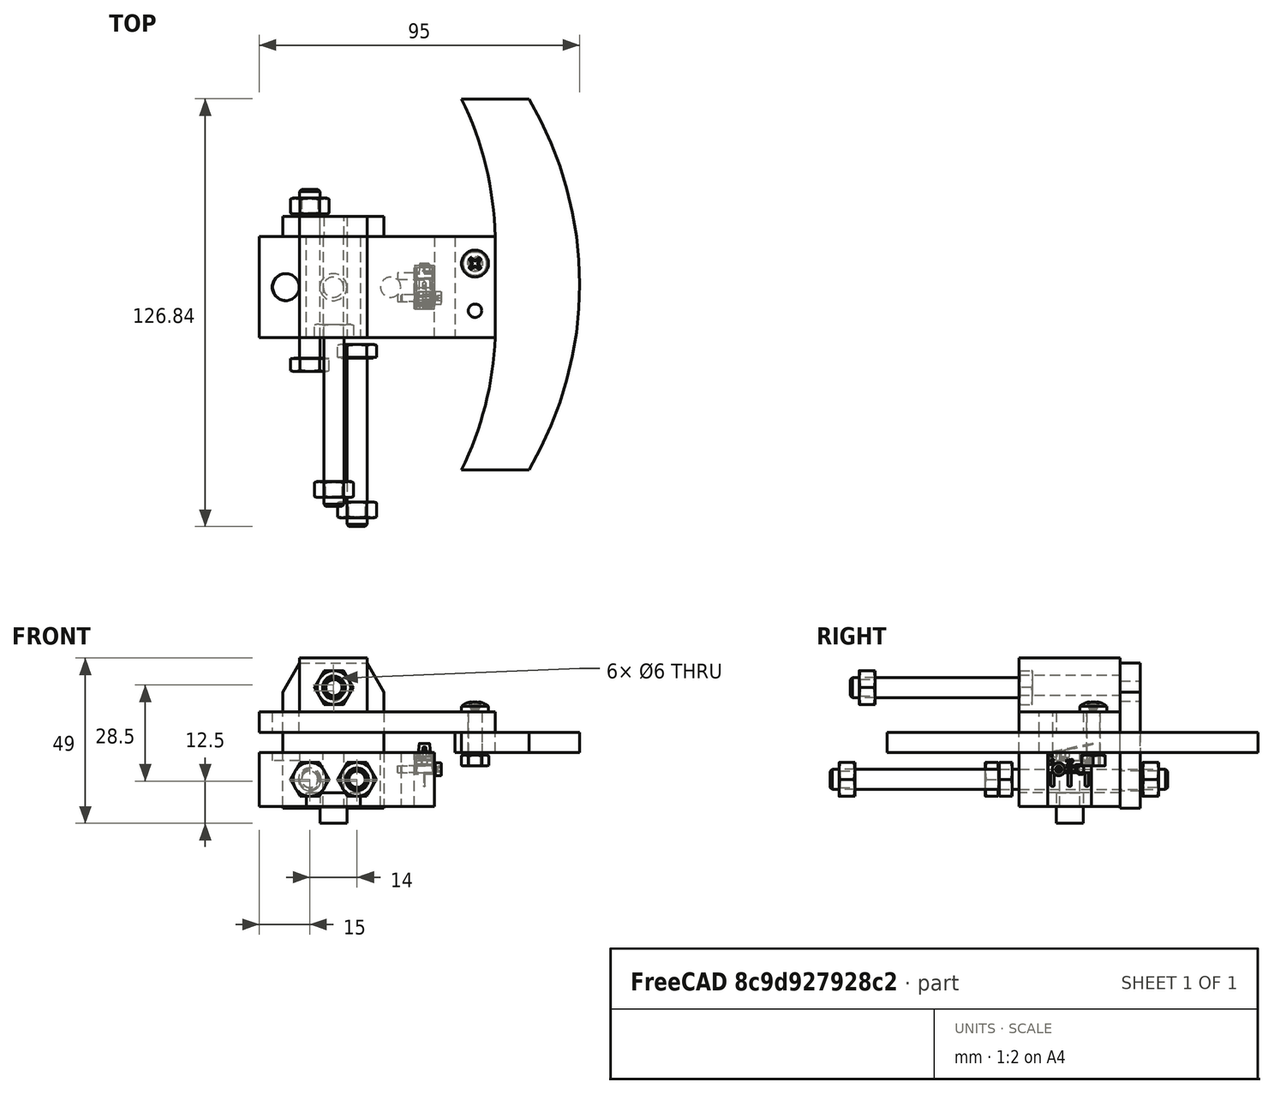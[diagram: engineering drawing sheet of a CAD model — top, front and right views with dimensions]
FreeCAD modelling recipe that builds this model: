
FCSTD DOCUMENT  (FreeCAD 0.19R24267 +99 (Git))
Label: PaddleShifter-v2
License: All rights reserved
LicenseURL: http://en.wikipedia.org/wiki/All_rights_reserved
objects: TechDraw::DrawViewDimension×44, Sketcher::SketchObject×14, Part::FeaturePython×12, TechDraw::DrawProjGroupItem×12, PartDesign::Pocket×10, TechDraw::DrawProjGroup×8, PartDesign::Pad×7, PartDesign::Body×7, PartDesign::SubShapeBinder×3, App::Part×3, PartDesign::ShapeBinder×2, Part::Feature×1, TechDraw::DrawSVGTemplate×1, App::MeasureDistance×1, TechDraw::DrawPage×1, App::DocumentObjectGroup×1
note: 73 computed .brp shape members not serialized (recipe doc carries the construction recipe); baked Part::Feature solids carry a one-line shape summary decoded from their .brp

FEATURE [Part::FeaturePython] Screw006  label="M2x10-Screw001"  # Fasteners workbench fastener (typed FeaturePython)
  Placement = pos=(30,-3.25,11) rot=(0,1,0;1.5708rad)
  baseObject = -> Body [Edge35]
  diameter = 2
  invert = false
  length = 5
  lengthCustom = 10
  matchOuter = true
  offset = 6
  thread = false
  type = 34
FEATURE [Part::FeaturePython] Screw005  label="M2x10-Screw"  # Fasteners workbench fastener (typed FeaturePython)
  Placement = pos=(30,-3.25,11) rot=(0,1,0;1.5708rad)
  baseObject = -> Body [Edge34]
  diameter = 2
  invert = false
  length = 5
  lengthCustom = 10
  matchOuter = true
  offset = 6
  thread = false
  type = 34
FEATURE [Part::FeaturePython] Nut004  label="M6-Nut168"  # Fasteners workbench fastener (typed FeaturePython)
  Placement = pos=(-7,26.3866,8) rot=(1,0,0;1.5708rad)
  baseObject = -> Screw003 [Edge39]
  diameter = 8
  invert = false
  matchOuter = true
  offset = 2
  thread = false
  type = 7
FEATURE [Part::FeaturePython] Nut003  label="M6-Nut167"  # Fasteners workbench fastener (typed FeaturePython)
  Placement = pos=(0.144842,-62.3866,35.2333) rot=(-1,0,0;1.5708rad)
  baseObject = -> Screw004 [Edge39]
  diameter = 8
  invert = false
  matchOuter = true
  offset = 2
  thread = false
  type = 7
FEATURE [Part::FeaturePython] Nut002  label="M6-Nut"  # Fasteners workbench fastener (typed FeaturePython)
  Placement = pos=(7,-68.3866,8) rot=(-1,0,0;1.5708rad)
  baseObject = -> Screw002 [Edge39]
  diameter = 8
  invert = false
  matchOuter = true
  offset = 2
  thread = false
  type = 7
FEATURE [Part::FeaturePython] Screw004  label="M6x50-Screw160"  # Fasteners workbench fastener (typed FeaturePython)
  Placement = pos=(0.144842,-15,35.2333) rot=(-1,0,0;1.5708rad)
  baseObject = -> Body001 [Edge16]
  diameter = 8
  invert = false
  length = 9
  lengthCustom = 50
  matchOuter = true
  offset = 0
  thread = false
  type = 29
FEATURE [Part::FeaturePython] Screw003  label="M6x50-Screw159"  # Fasteners workbench fastener (typed FeaturePython)
  Placement = pos=(-7,-21,8) rot=(1,0,0;1.5708rad)
  baseObject = -> Body001 [Edge17]
  diameter = 8
  invert = false
  length = 9
  lengthCustom = 50
  matchOuter = true
  offset = 0
  thread = false
  type = 29
FEATURE [Part::FeaturePython] Screw002  label="M6x50-Screw"  # Fasteners workbench fastener (typed FeaturePython)
  Placement = pos=(7,-21,8) rot=(-1,0,0;1.5708rad)
  baseObject = -> Body001 [Edge18]
  diameter = 8
  invert = true
  length = 9
  lengthCustom = 50
  matchOuter = true
  offset = 0
  thread = false
  type = 29
FEATURE [Part::Feature] Part__Feature  label="Switch"
  Placement = pos=(27,1.5e-14,9.5) rot=(0,0,1;1.5708rad)
  shape: bbox 7.341 x 13.39 x 13 mm, 256 faces, 7 solids (baked)
FEATURE [PartDesign::ShapeBinder] ShapeBinder001
  Placement = pos=(27,1.5e-14,9.5) rot=(0,0,1;1.5708rad)
  Support = -> [Part__Feature]
  TraceSupport = false
FEATURE [Sketcher::SketchObject] Sketch
  FullyConstrained = true
  MapMode = 5
  Support = -> [XY_Plane001]
  sketch-geometry (10):
    g0: LineSegment StartX=-22 StartY=15 StartZ=0 EndX=30 EndY=15 EndZ=0
    g1: LineSegment StartX=30 StartY=-15 StartZ=0 EndX=-22 EndY=-15 EndZ=0
    g2: LineSegment StartX=-22 StartY=-15 StartZ=0 EndX=-22 EndY=15 EndZ=0
    g3: GeomPoint X=0 Y=15 Z=0
    g4: GeomPoint X=-22 Y=0 Z=0
    g5: LineSegment StartX=30 StartY=15 StartZ=0 EndX=30 EndY=6.5 EndZ=0
    g6: LineSegment StartX=30 StartY=-15 StartZ=0 EndX=30 EndY=-6.5 EndZ=0
    g7: LineSegment StartX=30 StartY=-6.5 StartZ=0 EndX=24 EndY=-6.5 EndZ=0
    g8: LineSegment StartX=24 StartY=-6.5 StartZ=0 EndX=24 EndY=6.5 EndZ=0
    g9: LineSegment StartX=24 StartY=6.5 StartZ=0 EndX=30 EndY=6.5 EndZ=0
  constraints (27):
    c: Coincident(g1,g2)
    c: Coincident(g2,g0)
    c: Horizontal(g0)
    c: Horizontal(g1)
    c: Vertical(g2)
    c: DistanceY(g1,g0) = 30
    c: PointOnObject(g3,g-2)
    c: PointOnObject(g3,g0)
    c: Distance(g3,g0) = 22
    c: Distance(g3,g0) = 30
    c: PointOnObject(g4,g-1)
    c: Symmetric(g0,g1,g4)
    c: Coincident(g5,g0)
    c: Vertical(g5)
    c: Coincident(g6,g1)
    c: Vertical(g6)
    c: Coincident(g7,g6)
    c: Horizontal(g7)
    c: Coincident(g8,g7)
    c: Vertical(g8)
    c: Coincident(g9,g8)
    c: Coincident(g9,g5)
    c: Horizontal(g9)
    c: DistanceY(g8,g8) = 13
    c: Equal(g7,g9)
    c: Equal(g5,g6)
    c: DistanceX(g7,g7) = 6
FEATURE [PartDesign::Pad] Pad
  Direction = (1,1,1)
  Length = 16
  Length2 = 100
  Profile = -> Sketch
  Type = 0
FEATURE [Sketcher::SketchObject] Sketch001
  FullyConstrained = true
  MapMode = 5
  Support = -> [XY_Plane002]
  sketch-geometry (9):
    g0: LineSegment StartX=-15 StartY=21.5 StartZ=0 EndX=15 EndY=21.5 EndZ=0
    g1: LineSegment StartX=15 StartY=21.5 StartZ=0 EndX=15 EndY=-21.5 EndZ=0
    g2: LineSegment StartX=15 StartY=-21.5 StartZ=0 EndX=-15 EndY=-21.5 EndZ=0
    g3: LineSegment StartX=-15 StartY=-21.5 StartZ=0 EndX=-15 EndY=21.5 EndZ=0
    g4: LineSegment StartX=-15 StartY=-21.5 StartZ=0 EndX=-15 EndY=12.8397 EndZ=0
    g5: LineSegment StartX=-15 StartY=12.8397 StartZ=0 EndX=-10 EndY=21.5 EndZ=0
    g6: LineSegment StartX=-10 StartY=21.5 StartZ=0 EndX=10 EndY=21.5 EndZ=0
    g7: LineSegment StartX=10 StartY=21.5 StartZ=0 EndX=15 EndY=12.8397 EndZ=0
    g8: LineSegment StartX=15 StartY=12.8397 StartZ=0 EndX=15 EndY=-21.5 EndZ=0
  constraints (25):
    c: Coincident(g0,g1)
    c: Coincident(g1,g2)
    c: Coincident(g2,g3)
    c: Coincident(g3,g0)
    c: Horizontal(g0)
    c: Horizontal(g2)
    c: Vertical(g1)
    c: Vertical(g3)
    c: Symmetric(g2,g0,g-1)
    c: DistanceX(g0,g0) = 30
    c: DistanceY(g1,g1) = 43
    c: Coincident(g4,g2)
    c: PointOnObject(g4,g3)
    c: Coincident(g5,g4)
    c: PointOnObject(g5,g0)
    c: Coincident(g6,g5)
    c: PointOnObject(g6,g0)
    c: Coincident(g7,g6)
    c: PointOnObject(g7,g1)
    c: Coincident(g8,g7)
    c: Coincident(g8,g2)
    c: Equal(g4,g8)
    c: Equal(g5,g7)
    c: Distance(g6) = 20
    c: Distance(g7) = 10
FEATURE [PartDesign::Pad] Pad001
  Direction = (1,1,1)
  Length = 6
  Length2 = 100
  Profile = -> Sketch001
  Type = 0
FEATURE [PartDesign::SubShapeBinder] Binder
  BindMode = 0
  ClaimChildren = false
  Context = -> Part [Body001.Binder.]
  Fuse = false
  MakeFace = true
  PartialLoad = false
  Relative = true
  Support = -> [Part001[Body004.Pocket002.Edge15]]
  _Version = 2
FEATURE [PartDesign::Pocket] Pocket008
  BaseFeature = -> Pad001
  Length = 5
  Length2 = 100
  Profile = -> Binder
  Reversed = true
  Type = 1
FEATURE [Sketcher::SketchObject] Sketch012
  FullyConstrained = false
  MapMode = 5
  Support = -> [XY_Plane009]
  sketch-geometry (13):
    g0: LineSegment StartX=-10 StartY=55 StartZ=0 EndX=10 EndY=55 EndZ=0
    g1: LineSegment StartX=10 StartY=55 StartZ=0 EndX=10 EndY=-55 EndZ=0
    g2: LineSegment StartX=10 StartY=-55 StartZ=0 EndX=-10 EndY=-55 EndZ=0
    g3: LineSegment StartX=-10 StartY=-55 StartZ=0 EndX=-10 EndY=55 EndZ=0
    g4: LineSegment StartX=10 StartY=55 StartZ=0 EndX=-10 EndY=55 EndZ=0
    g5: LineSegment StartX=0 StartY=14.1646 StartZ=0 EndX=-12 EndY=14.1646 EndZ=0
    g6: LineSegment StartX=7e-16 StartY=-15.8354 StartZ=0 EndX=-12 EndY=-15.8354 EndZ=0
    g7: LineSegment StartX=-12 StartY=14.1646 StartZ=0 EndX=-12 EndY=-15.8354 EndZ=0
    g8: LineSegment StartX=10 StartY=-55 StartZ=0 EndX=-10 EndY=-55 EndZ=0
    g9: ArcOfCircle CenterX=-83.3333 CenterY=1e-15 CenterZ=0 NormalX=0 NormalY=0 NormalZ=1 AngleXU=0 Radius=108.333 StartAngle=5.75068 EndAngle=6.81569
    g10: ArcOfCircle CenterX=-98.5179 CenterY=-11.5395 CenterZ=0 NormalX=0 NormalY=0 NormalZ=1 AngleXU=0 Radius=98.6115 StartAngle=5.82678 EndAngle=6.23961
    g11: ArcOfCircle CenterX=-98.5798 CenterY=11.666 CenterZ=0 NormalX=0 NormalY=0 NormalZ=1 AngleXU=0 Radius=98.6115 StartAngle=0.025341 EndAngle=0.454978
    g12: GeomPoint X=25 Y=0 Z=0
  constraints (34):
    c: Coincident(g0,g1)
    c: Coincident(g2,g3)
    c: Coincident(g3,g0)
    c: Horizontal(g0)
    c: Horizontal(g2)
    c: Coincident(g7,g5)
    c: Coincident(g7,g6)
    c: Equal(g5,g6)
    c: Vertical(g7)
    c: Coincident(g8,g2)
    c: Horizontal(g5)
    c: Horizontal(g6)
    c: Coincident(g4,g0)
    c: DistanceX(g0,g0) = 20
    c: PointOnObject(g5,g-2)
    c: DistanceY(g7,g7) = 30
    c: Coincident(g9,g4)
    c: Vertical(g3)
    c: Vertical(g1)
    c: Coincident(g10,g6)
    c: Coincident(g10,g8)
    c: Coincident(g11,g4)
    c: Coincident(g11,g5)
    c: Equal(g11,g10)
    c: DistanceY(g8,g4) = 110
    c: PointOnObject(g12,g9)
    c: PointOnObject(g12,g-1)
    c: Distance(g-1,g12) = 25
    c: DistanceX(g5,g5) = 12
    c: Coincident(g8,g1)
    c: Coincident(g8,g9)
    c: Coincident(g8,g2)
    c: Coincident(g4,g0)
    c: Symmetric(g8,g4,g-1)
FEATURE [PartDesign::Pad] Pad006
  Direction = (1,1,1)
  Length = 6
  Length2 = 100
  Profile = -> Sketch012
  Type = 0
FEATURE [Sketcher::SketchObject] Sketch014
  ExternalGeometry = -> [Pad006]
  FullyConstrained = true
  MapMode = 5
  Placement = pos=(0,0,6) rot=(0,0,1;0rad)
  Support = -> [Pad006]
  sketch-geometry (3):
    g0: Circle CenterX=-6 CenterY=6.1646 CenterZ=0 NormalX=0 NormalY=0 NormalZ=1 AngleXU=0 Radius=2
    g1: Circle CenterX=-6 CenterY=-7.8354 CenterZ=0 NormalX=0 NormalY=0 NormalZ=1 AngleXU=0 Radius=2
    g2: LineSegment StartX=-6 StartY=14.1646 StartZ=0 EndX=-6 EndY=-15.8354 EndZ=0
  constraints (10):
    c: Equal(g0,g1)
    c: Diameter(g0) = 4
    c: PointOnObject(g2,g-3)
    c: PointOnObject(g2,g-5)
    c: Vertical(g2)
    c: PointOnObject(g0,g2)
    c: PointOnObject(g1,g2)
    c: Distance(g0,g2) = 8
    c: Distance(g1,g2) = 8
    c: Distance(g2,g-4) = 6
FEATURE [PartDesign::Pocket] Pocket007
  BaseFeature = -> Pad006
  Length = 5
  Length2 = 100
  Profile = -> Sketch014
  Type = 1
FEATURE [PartDesign::Body] Body006  label="Лепесток"
  Group = -> [Sketch012,Pad006,Sketch014,Pocket007]
  Origin = -> Origin009
  Placement = pos=(48,0.8354,16) rot=(0,0,1;0rad)
  Tip = -> Pocket007
FEATURE [Sketcher::SketchObject] Sketch007
  FullyConstrained = true
  MapMode = 5
  Support = -> [XY_Plane005]
  sketch-geometry (4):
    g0: LineSegment StartX=-10 StartY=15 StartZ=0 EndX=10 EndY=15 EndZ=0
    g1: LineSegment StartX=10 StartY=15 StartZ=0 EndX=10 EndY=-15 EndZ=0
    g2: LineSegment StartX=10 StartY=-15 StartZ=0 EndX=-10 EndY=-15 EndZ=0
    g3: LineSegment StartX=-10 StartY=-15 StartZ=0 EndX=-10 EndY=15 EndZ=0
  constraints (11):
    c: Coincident(g0,g1)
    c: Coincident(g1,g2)
    c: Coincident(g2,g3)
    c: Coincident(g3,g0)
    c: Horizontal(g0)
    c: Horizontal(g2)
    c: Vertical(g1)
    c: Vertical(g3)
    c: Symmetric(g0,g2,g-1)
    c: DistanceX(g0,g0) = 20
    c: DistanceY(g1,g1) = 30
FEATURE [PartDesign::Pad] Pad004
  Direction = (1,1,1)
  Length = 16
  Length2 = 100
  Profile = -> Sketch007
  Type = 0
FEATURE [Sketcher::SketchObject] Sketch008
  ExternalGeometry = -> [Pad004]
  FullyConstrained = true
  MapMode = 5
  Placement = pos=(0,15,0) rot=(0,0.707107,0.707107;3.14159rad)
  Support = -> [Pad004]
  sketch-geometry (1):
    g0: Circle CenterX=1.1e-15 CenterY=8 CenterZ=0 NormalX=0 NormalY=0 NormalZ=1 AngleXU=0 Radius=3
  constraints (2):
    c: Diameter(g0) = 6
    c: Symmetric(g-3,g-5,g0)
FEATURE [PartDesign::Pocket] Pocket002
  BaseFeature = -> Pad004
  Length = 5
  Length2 = 100
  Profile = -> Sketch008
  Type = 1
FEATURE [PartDesign::Body] Body004  label="Крепление рычага"
  Group = -> [Sketch007,Pad004,Sketch008,Pocket002]
  Origin = -> Origin005
  Placement = pos=(0,0,28) rot=(0,0,1;0rad)
  Tip = -> Pocket002
FEATURE [Sketcher::SketchObject] Sketch005
  FullyConstrained = true
  MapMode = 5
  Support = -> [XY_Plane003]
  sketch-geometry (4):
    g0: LineSegment StartX=-35 StartY=15 StartZ=0 EndX=35 EndY=15 EndZ=0
    g1: LineSegment StartX=35 StartY=15 StartZ=0 EndX=35 EndY=-15 EndZ=0
    g2: LineSegment StartX=35 StartY=-15 StartZ=0 EndX=-35 EndY=-15 EndZ=0
    g3: LineSegment StartX=-35 StartY=-15 StartZ=0 EndX=-35 EndY=15 EndZ=0
  constraints (11):
    c: Coincident(g0,g1)
    c: Coincident(g1,g2)
    c: Coincident(g2,g3)
    c: Coincident(g3,g0)
    c: Horizontal(g0)
    c: Horizontal(g2)
    c: Vertical(g1)
    c: Vertical(g3)
    c: Symmetric(g0,g2,g-1)
    c: DistanceY(g1,g1) = 30
    c: DistanceX(g0,g0) = 70
FEATURE [PartDesign::Pad] Pad002
  Direction = (1,1,1)
  Length = 6
  Length2 = 100
  Profile = -> Sketch005
  Type = 0
FEATURE [PartDesign::SubShapeBinder] Binder001
  BindMode = 0
  ClaimChildren = false
  Context = -> Part [Part001.Body002.Binder001.]
  Fuse = false
  MakeFace = true
  PartialLoad = false
  Relative = true
  Support = -> [Part002[Body003.Pad003.Edge15]]
  _Version = 2
FEATURE [PartDesign::Pocket] Pocket004
  BaseFeature = -> Pad002
  Length = 5
  Length2 = 100
  Profile = -> Binder001
  Reversed = true
  Type = 1
FEATURE [Sketcher::SketchObject] Sketch013
  ExternalGeometry = -> [Pocket004]
  FullyConstrained = false
  MapMode = 5
  Placement = pos=(0,0,6) rot=(0,0,1;0rad)
  Support = -> [Pocket004]
  sketch-geometry (3):
    g0: Circle CenterX=29 CenterY=7 CenterZ=0 NormalX=0 NormalY=0 NormalZ=1 AngleXU=0 Radius=2
    g1: Circle CenterX=29 CenterY=-7 CenterZ=0 NormalX=0 NormalY=0 NormalZ=1 AngleXU=0 Radius=2
    g2: LineSegment StartX=29 StartY=15 StartZ=0 EndX=29 EndY=-15 EndZ=0
  constraints (9):
    c: Diameter(g0) = 4
    c: Equal(g0,g1)
    c: PointOnObject(g2,g-3)
    c: Vertical(g2)
    c: PointOnObject(g0,g2)
    c: PointOnObject(g1,g2)
    c: Distance(g0,g2) = 8
    c: Distance(g1,g2) = 8
    c: Distance(g2,g-3) = 6
FEATURE [PartDesign::Pocket] Pocket006
  BaseFeature = -> Pocket004
  Length = 5
  Length2 = 100
  Profile = -> Sketch013
  Type = 1
FEATURE [PartDesign::Body] Body002  label="Рычаг"
  Group = -> [Sketch005,Pad002,Binder001,Pocket004,Sketch013,Pocket006]
  Origin = -> Origin003
  Placement = pos=(13,0,22) rot=(0,0,1;0rad)
  Tip = -> Pocket006
FEATURE [Sketcher::SketchObject] Sketch006
  FullyConstrained = true
  MapMode = 5
  Support = -> [XY_Plane004]
  sketch-geometry (5):
    g0: LineSegment StartX=-8 StartY=15 StartZ=0 EndX=8 EndY=15 EndZ=0
    g1: LineSegment StartX=8 StartY=15 StartZ=0 EndX=8 EndY=-15 EndZ=0
    g2: LineSegment StartX=8 StartY=-15 StartZ=0 EndX=-8 EndY=-15 EndZ=0
    g3: LineSegment StartX=-8 StartY=-15 StartZ=0 EndX=-8 EndY=15 EndZ=0
    g4: Circle CenterX=0 CenterY=0 CenterZ=0 NormalX=0 NormalY=0 NormalZ=1 AngleXU=0 Radius=4
  constraints (13):
    c: Coincident(g0,g1)
    c: Coincident(g1,g2)
    c: Coincident(g2,g3)
    c: Coincident(g3,g0)
    c: Horizontal(g0)
    c: Horizontal(g2)
    c: Vertical(g1)
    c: Vertical(g3)
    c: Symmetric(g0,g2,g-1)
    c: DistanceX(g0,g0) = 16
    c: DistanceY(g1,g1) = 30
    c: Coincident(g4,g-1)
    c: Diameter(g4) = 8
FEATURE [PartDesign::Pad] Pad003
  Direction = (1,1,1)
  Length = 4
  Length2 = 100
  Midplane = true
  Profile = -> Sketch006
  Type = 0
FEATURE [PartDesign::Body] Body003  label="Проставка"
  Group = -> [Sketch006,Pad003]
  Origin = -> Origin004
  Placement = pos=(0,0,2) rot=(0,0,1;0rad)
  Tip = -> Pad003
FEATURE [Sketcher::SketchObject] Sketch010
  FullyConstrained = true
  MapMode = 5
  Support = -> [XY_Plane007]
  sketch-geometry (1):
    g0: Circle CenterX=0 CenterY=0 CenterZ=0 NormalX=0 NormalY=0 NormalZ=1 AngleXU=0 Radius=4
  constraints (2):
    c: Coincident(g0,g-1)
    c: Diameter(g0) = 8
FEATURE [PartDesign::Pad] Pad005
  Direction = (1,1,1)
  Length = 5
  Length2 = 100
  Profile = -> Sketch010
  Type = 0
FEATURE [PartDesign::Body] Body005  label="Неодимовый магнит (8х5)"
  Group = -> [Sketch010,Pad005]
  Origin = -> Origin007
  Placement = pos=(-14,0,22) rot=(0,0,1;0rad)
  Tip = -> Pad005
FEATURE [Part::FeaturePython] Clone  label="Неодимовый магнит (8х5)001"  # Draft clone (typed FeaturePython)
  AttacherType = Attacher::AttachEngine3D
  Fuse = false
  Objects = -> [Body005]
  Placement = pos=(4e-15,0,-5) rot=(0,0,1;0rad)
  Scale = (1,1,1)
FEATURE [App::Part] Part002  label="Проставка001"
  Group = -> [Clone,Body003]
  Origin = -> Origin008
  Placement = pos=(-14,0,16) rot=(0,0,1;0rad)
FEATURE [Part::FeaturePython] Screw  label="M4x16-Screw"  # Fasteners workbench fastener (typed FeaturePython)
  Placement = pos=(42,7,28) rot=(0,0,1;0rad)
  baseObject = -> Body002 [Edge18]
  diameter = 6
  invert = false
  length = 6
  lengthCustom = 16
  matchOuter = false
  offset = 0
  thread = false
  type = 35
FEATURE [Part::FeaturePython] Nut005  label="M4-Nut"  # Fasteners workbench fastener (typed FeaturePython)
  Placement = pos=(42,7,12) rot=(0,0,1;0rad)
  baseObject = -> Screw [Edge7]
  diameter = 6
  invert = false
  matchOuter = false
  offset = 0
  thread = false
  type = 7
FEATURE [App::Part] Part001  label="Рычаг001"
  Group = -> [Body002,Body004,Body005,Body006,Screw,Nut005]
  Origin = -> Origin006
  Placement = pos=(0.144842,0,-0.766663) rot=(0,0,1;0rad)
FEATURE [PartDesign::SubShapeBinder] Binder002
  BindMode = 0
  ClaimChildren = false
  Context = -> Part [Body.Binder002.]
  Fuse = false
  MakeFace = true
  PartialLoad = false
  Relative = true
  Support = -> [Part002[Body003.Pad003.Edge14]]
  _Version = 2
FEATURE [Sketcher::SketchObject] Sketch015
  ExternalGeometry = -> [Pocket008]
  FullyConstrained = true
  MapMode = 5
  Placement = pos=(0,0,6) rot=(0,0,1;0rad)
  Support = -> [Pocket008]
  sketch-geometry (3):
    g0: LineSegment StartX=-15 StartY=-13.5 StartZ=0 EndX=15 EndY=-13.5 EndZ=0
    g1: Circle CenterX=-7 CenterY=-13.5 CenterZ=0 NormalX=0 NormalY=0 NormalZ=1 AngleXU=0 Radius=3
    g2: Circle CenterX=7 CenterY=-13.5 CenterZ=0 NormalX=0 NormalY=0 NormalZ=1 AngleXU=0 Radius=3
  constraints (10):
    c: PointOnObject(g0,g-3)
    c: PointOnObject(g0,g-5)
    c: Horizontal(g0)
    c: PointOnObject(g1,g0)
    c: PointOnObject(g2,g0)
    c: Equal(g2,g1)
    c: Diameter(g2) = 6
    c: DistanceY(g-5,g0) = 8
    c: Distance(g2,g-5) = 8
    c: Distance(g1,g-3) = 8
FEATURE [PartDesign::Pocket] Pocket
  BaseFeature = -> Pocket008
  Length = 5
  Length2 = 100
  Profile = -> Sketch015
  Type = 1
FEATURE [PartDesign::Body] Body001  label="Крепление"
  Group = -> [Sketch001,Pad001,Binder,Pocket008,Sketch015,Pocket]
  Origin = -> Origin002
  Placement = pos=(-3e-15,-15,22) rot=(1,0,0;1.5708rad)
  Tip = -> Pocket
FEATURE [PartDesign::ShapeBinder] ShapeBinder
  Placement = pos=(-3e-15,-15,22) rot=(1,0,0;1.5708rad)
  Support = -> [Body001]
  TraceSupport = false
FEATURE [Sketcher::SketchObject] Sketch004
  ExternalGeometry = -> [ShapeBinder]
  FullyConstrained = false
  MapMode = 5
  Placement = pos=(0,15,0) rot=(0,0.707107,0.707107;3.14159rad)
  Support = -> [Pad]
  sketch-geometry (3):
    g0: Circle CenterX=7 CenterY=8 CenterZ=0 NormalX=0 NormalY=0 NormalZ=1 AngleXU=0 Radius=3
    g1: Circle CenterX=-9e-16 CenterY=31 CenterZ=0 NormalX=0 NormalY=0 NormalZ=1 AngleXU=0 Radius=3
    g2: Circle CenterX=-7 CenterY=8 CenterZ=0 NormalX=0 NormalY=0 NormalZ=1 AngleXU=0 Radius=3
FEATURE [PartDesign::Pocket] Pocket001
  BaseFeature = -> Pad
  Length = 5
  Length2 = 100
  Profile = -> Sketch004
  Type = 1
FEATURE [Sketcher::SketchObject] Sketch009
  ExternalGeometry = -> [Pocket001]
  FullyConstrained = true
  MapMode = 5
  Placement = pos=(0,0,16) rot=(0,0,1;0rad)
  Support = -> [Pocket001]
  sketch-geometry (2):
    g0: Circle CenterX=0 CenterY=0 CenterZ=0 NormalX=0 NormalY=0 NormalZ=1 AngleXU=0 Radius=3
    g1: Circle CenterX=17 CenterY=0 CenterZ=0 NormalX=0 NormalY=0 NormalZ=1 AngleXU=0 Radius=3
  constraints (5):
    c: Diameter(g0) = 6
    c: PointOnObject(g1,g-1)
    c: Equal(g0,g1)
    c: Distance(g1,g-6) = 13
    c: Coincident(g0,g-1)
FEATURE [PartDesign::Pocket] Pocket003
  BaseFeature = -> Pocket001
  Length = 5
  Length2 = 100
  Profile = -> Sketch009
  Type = 1
FEATURE [Sketcher::SketchObject] Sketch011
  ExternalGeometry = -> [Pocket003]
  FullyConstrained = true
  MapMode = 5
  Placement = pos=(24,0,0) rot=(0.57735,0.57735,0.57735;2.0944rad)
  Support = -> [Pocket003]
  sketch-geometry (3):
    g0: Circle CenterX=3.25 CenterY=11 CenterZ=0 NormalX=0 NormalY=0 NormalZ=1 AngleXU=0 Radius=1
    g1: Circle CenterX=-3.25 CenterY=11 CenterZ=0 NormalX=0 NormalY=0 NormalZ=1 AngleXU=0 Radius=1
    g2: LineSegment StartX=-3.25 StartY=11 StartZ=0 EndX=3.25 EndY=11 EndZ=0
  constraints (8):
    c: Diameter(g0) = 2
    c: DistanceX(g-2,g0) = 3.25
    c: Equal(g1,g0)
    c: Coincident(g2,g1)
    c: Coincident(g2,g0)
    c: Horizontal(g2)
    c: DistanceX(g-2,g1) = -3.25
    c: Distance(g1,g-3) = 5
FEATURE [PartDesign::Pocket] Pocket005
  BaseFeature = -> Pocket003
  Length = 5
  Length2 = 100
  Profile = -> Sketch011
  Type = 0
FEATURE [Part::FeaturePython] Clone001  label="Крепление001"  # Draft clone (typed FeaturePython)
  AttacherType = Attacher::AttachEngine3D
  Fuse = false
  Objects = -> [Body001]
  Placement = pos=(-3e-15,21,21) rot=(1,0,0;1.5708rad)
  Scale = (1,1,1)
FEATURE [PartDesign::Pocket] Pocket009
  BaseFeature = -> Pocket005
  Length = 5
  Length2 = 100
  Midplane = true
  Profile = -> Binder002
  Type = 0
FEATURE [PartDesign::Body] Body  label="Основа"
  Group = -> [Sketch,Pad,ShapeBinder,Sketch004,Pocket001,Sketch009,Pocket003,ShapeBinder001,Sketch011,Pocket005,Binder002,Pocket009]
  Origin = -> Origin001
  Tip = -> Pocket009
FEATURE [App::Part] Part  label="PaddleShifter"
  Group = -> [Body,Body001,Part__Feature,Part001,Part002,Screw002,Screw003,Screw004,Nut002,Nut003,Nut004,Screw005,Screw006,Clone001]
  Origin = -> Origin
FEATURE [TechDraw::DrawSVGTemplate] Template
  Height = 210
  Orientation = 1
  Width = 297
FEATURE [TechDraw::DrawProjGroupItem] ProjItem  label="Front"
  CoarseView = false
  Direction = (0,-1,0)
  Focus = 100
  HardHidden = false
  IsoCount = 0
  IsoHidden = false
  IsoVisible = false
  LockPosition = true
  Perspective = false
  Rotation = 0
  RotationVector = (1,0,0)
  ScaleType = 2
  SeamHidden = false
  SeamVisible = true
  SmoothHidden = false
  SmoothVisible = true
  Source = -> [Body001]
  Type = 0
  X = 0
  XDirection = (1,0,0)
  Y = 0
FEATURE [TechDraw::DrawProjGroupItem] ProjItem001  label="Left"
  CoarseView = false
  Direction = (-1,-1e-16,0)
  Focus = 100
  HardHidden = false
  IsoCount = 0
  IsoHidden = false
  IsoVisible = false
  LockPosition = false
  Perspective = false
  Rotation = 0
  RotationVector = (1,0,0)
  ScaleType = 2
  SeamHidden = false
  SeamVisible = true
  SmoothHidden = false
  SmoothVisible = true
  Source = -> [Body001]
  Type = 1
  X = 33
  XDirection = (1e-16,-1,0)
  Y = 0
FEATURE [TechDraw::DrawProjGroup] ProjGroup
  Anchor = -> ProjItem
  AutoDistribute = true
  LockPosition = false
  ProjectionType = 0
  Rotation = 0
  ScaleType = 0
  Source = -> [Body001]
  Views = -> [ProjItem,ProjItem001]
  X = 43.5
  Y = 172.616
  spacingX = 15
  spacingY = 15
FEATURE [TechDraw::DrawProjGroupItem] ProjItem002  label="Front001"
  CoarseView = false
  Direction = (0,-1,0)
  Focus = 100
  HardHidden = false
  IsoCount = 0
  IsoHidden = false
  IsoVisible = false
  LockPosition = true
  Perspective = false
  Rotation = 0
  RotationVector = (1,0,0)
  ScaleType = 2
  SeamHidden = false
  SeamVisible = true
  SmoothHidden = false
  SmoothVisible = true
  Source = -> [Body]
  Type = 0
  X = 0
  XDirection = (1,0,0)
  Y = 0
FEATURE [TechDraw::DrawProjGroupItem] ProjItem004  label="Front002"
  CoarseView = false
  Direction = (0,0,1)
  Focus = 100
  HardHidden = false
  IsoCount = 0
  IsoHidden = false
  IsoVisible = false
  LockPosition = true
  Perspective = false
  Rotation = 0
  RotationVector = (1,0,0)
  ScaleType = 2
  SeamHidden = false
  SeamVisible = true
  SmoothHidden = false
  SmoothVisible = true
  Source = -> [Body004]
  Type = 0
  X = 0
  XDirection = (1,0,0)
  Y = 0
FEATURE [TechDraw::DrawProjGroupItem] ProjItem005  label="Top"
  CoarseView = false
  Direction = (0,1,0)
  Focus = 100
  HardHidden = false
  IsoCount = 0
  IsoHidden = false
  IsoVisible = false
  LockPosition = false
  Perspective = false
  Rotation = 0
  RotationVector = (1,0,0)
  ScaleType = 2
  SeamHidden = false
  SeamVisible = true
  SmoothHidden = false
  SmoothVisible = true
  Source = -> [Body004]
  Type = 4
  X = 0
  XDirection = (1,0,0)
  Y = -52
FEATURE [TechDraw::DrawProjGroup] ProjGroup002
  Anchor = -> ProjItem004
  AutoDistribute = true
  LockPosition = false
  ProjectionType = 0
  Rotation = 0
  ScaleType = 0
  Source = -> [Body004]
  Views = -> [ProjItem004,ProjItem005]
  X = 193.036
  Y = 170.341
  spacingX = 15
  spacingY = 15
FEATURE [TechDraw::DrawProjGroupItem] ProjItem006  label="Front003"
  CoarseView = false
  Direction = (0,0,1)
  Focus = 100
  HardHidden = false
  IsoCount = 0
  IsoHidden = false
  IsoVisible = false
  LockPosition = true
  Perspective = false
  Rotation = 0
  RotationVector = (1,0,0)
  ScaleType = 2
  SeamHidden = false
  SeamVisible = true
  SmoothHidden = false
  SmoothVisible = true
  Source = -> [Body002]
  Type = 0
  X = 0
  XDirection = (1,0,0)
  Y = 0
FEATURE [TechDraw::DrawProjGroup] ProjGroup003
  Anchor = -> ProjItem006
  AutoDistribute = true
  LockPosition = false
  ProjectionType = 0
  Rotation = 0
  ScaleType = 0
  Source = -> [Body002]
  Views = -> [ProjItem006]
  X = 61.3793
  Y = 113.127
  spacingX = 15
  spacingY = 15
FEATURE [TechDraw::DrawProjGroupItem] ProjItem007  label="Top001"
  CoarseView = false
  Direction = (0,0,1)
  Focus = 100
  HardHidden = false
  IsoCount = 0
  IsoHidden = false
  IsoVisible = false
  LockPosition = false
  Perspective = false
  Rotation = 0
  RotationVector = (1,0,0)
  ScaleType = 2
  SeamHidden = false
  SeamVisible = true
  SmoothHidden = false
  SmoothVisible = true
  Source = -> [Body]
  Type = 4
  X = 0
  XDirection = (1,0,0)
  Y = -45
FEATURE [TechDraw::DrawProjGroup] ProjGroup001
  Anchor = -> ProjItem002
  AutoDistribute = true
  LockPosition = false
  ProjectionType = 0
  Rotation = 0
  ScaleType = 0
  Source = -> [Body]
  Views = -> [ProjItem002,ProjItem007]
  X = 135.497
  Y = 122.554
  spacingX = 15
  spacingY = 15
FEATURE [TechDraw::DrawProjGroupItem] ProjItem008  label="Front004"
  CoarseView = false
  Direction = (0,0,1)
  Focus = 100
  HardHidden = false
  IsoCount = 0
  IsoHidden = false
  IsoVisible = false
  LockPosition = true
  Perspective = false
  Rotation = 0
  RotationVector = (1,0,0)
  ScaleType = 2
  SeamHidden = false
  SeamVisible = true
  SmoothHidden = false
  SmoothVisible = true
  Source = -> [Body006]
  Type = 0
  X = 0
  XDirection = (-2e-16,1,0)
  Y = 0
FEATURE [TechDraw::DrawProjGroup] ProjGroup004
  Anchor = -> ProjItem008
  AutoDistribute = true
  LockPosition = false
  ProjectionType = 0
  Rotation = 0
  ScaleType = 0
  Source = -> [Body006]
  Views = -> [ProjItem008]
  X = 71.2141
  Y = 35.5674
  spacingX = 15
  spacingY = 15
FEATURE [TechDraw::DrawProjGroupItem] ProjItem009  label="Front005"
  CoarseView = false
  Direction = (0,0,1)
  Focus = 100
  HardHidden = false
  IsoCount = 0
  IsoHidden = false
  IsoVisible = false
  LockPosition = true
  Perspective = false
  Rotation = 0
  RotationVector = (1,0,0)
  ScaleType = 2
  SeamHidden = false
  SeamVisible = true
  SmoothHidden = false
  SmoothVisible = true
  Source = -> [Part002]
  Type = 0
  X = 0
  XDirection = (1,0,0)
  Y = 0
FEATURE [TechDraw::DrawProjGroupItem] ProjItem010  label="Top002"
  CoarseView = false
  Direction = (0,1,0)
  Focus = 100
  HardHidden = false
  IsoCount = 0
  IsoHidden = false
  IsoVisible = false
  LockPosition = false
  Perspective = false
  Rotation = 0
  RotationVector = (1,0,0)
  ScaleType = 2
  SeamHidden = false
  SeamVisible = true
  SmoothHidden = false
  SmoothVisible = true
  Source = -> [Part002]
  Type = 4
  X = 0
  XDirection = (1,0,0)
  Y = -55.5
FEATURE [TechDraw::DrawProjGroup] ProjGroup005
  Anchor = -> ProjItem009
  AutoDistribute = true
  LockPosition = false
  ProjectionType = 0
  Rotation = 0
  ScaleType = 0
  Source = -> [Part002]
  Views = -> [ProjItem009,ProjItem010]
  X = 238.238
  Y = 169.811
  spacingX = 15
  spacingY = 15
FEATURE [TechDraw::DrawProjGroupItem] ProjItem011  label="Front006"
  CoarseView = false
  Direction = (0,0,1)
  Focus = 100
  HardHidden = false
  IsoCount = 0
  IsoHidden = false
  IsoVisible = false
  LockPosition = true
  Perspective = false
  Rotation = 0
  RotationVector = (1,0,0)
  ScaleType = 2
  SeamHidden = false
  SeamVisible = true
  SmoothHidden = false
  SmoothVisible = true
  Source = -> [Body006]
  Type = 0
  X = 0
  XDirection = (-2e-16,1,0)
  Y = 0
FEATURE [TechDraw::DrawProjGroup] ProjGroup006
  Anchor = -> ProjItem011
  AutoDistribute = true
  LockPosition = false
  ProjectionType = 0
  Rotation = 0
  ScaleType = 0
  Source = -> [Body006]
  Views = -> [ProjItem011]
  X = 209.746
  Y = 38.0976
  spacingX = 15
  spacingY = 15
FEATURE [TechDraw::DrawViewDimension] Dimension
  Arbitrary = false
  ArbitraryTolerances = false
  EqualTolerance = true
  FormatSpec = %.2f
  FormatSpecOverTolerance = %+.2f
  FormatSpecUnderTolerance = %+.2f
  Inverted = false
  LockPosition = false
  MeasureType = 1
  OverTolerance = 0
  References2D = -> [ProjItem]
  Rotation = 0
  ScaleType = 0
  TheoreticalExact = false
  Type = 2
  UnderTolerance = 0
  X = 19.8762
  Y = -4.33013
FEATURE [TechDraw::DrawViewDimension] Dimension002
  Arbitrary = false
  ArbitraryTolerances = false
  EqualTolerance = true
  FormatSpec = %.2f
  FormatSpecOverTolerance = %+.2f
  FormatSpecUnderTolerance = %+.2f
  Inverted = false
  LockPosition = false
  MeasureType = 1
  OverTolerance = 0
  References2D = -> [ProjItem]
  Rotation = 0
  ScaleType = 0
  TheoreticalExact = false
  Type = 2
  UnderTolerance = 0
  X = -21.9814
  Y = 0.270898
FEATURE [TechDraw::DrawViewDimension] Dimension003
  Arbitrary = false
  ArbitraryTolerances = false
  EqualTolerance = true
  FormatSpec = %.2f
  FormatSpecOverTolerance = %+.2f
  FormatSpecUnderTolerance = %+.2f
  Inverted = false
  LockPosition = false
  MeasureType = 1
  OverTolerance = 0
  References2D = -> [ProjItem]
  Rotation = 0
  ScaleType = 0
  TheoreticalExact = false
  Type = 2
  UnderTolerance = 0
  X = 19.2724
  Y = 17.5662
FEATURE [TechDraw::DrawViewDimension] Dimension004
  Arbitrary = false
  ArbitraryTolerances = false
  EqualTolerance = true
  FormatSpec = %.2f
  FormatSpecOverTolerance = %+.2f
  FormatSpecUnderTolerance = %+.2f
  Inverted = false
  LockPosition = false
  MeasureType = 1
  OverTolerance = 0
  References2D = -> [ProjItem]
  Rotation = 0
  ScaleType = 0
  TheoreticalExact = false
  Type = 1
  UnderTolerance = 0
  X = 0
  Y = -21.3739
FEATURE [TechDraw::DrawViewDimension] Dimension005
  Arbitrary = false
  ArbitraryTolerances = false
  EqualTolerance = true
  FormatSpec = ⌀%.2f
  FormatSpecOverTolerance = %+.2f
  FormatSpecUnderTolerance = %+.2f
  Inverted = false
  LockPosition = false
  MeasureType = 1
  OverTolerance = 0
  References2D = -> [ProjItem]
  Rotation = 0
  ScaleType = 0
  TheoreticalExact = false
  Type = 5
  UnderTolerance = 0
  X = -9.61702
  Y = 3.60638
FEATURE [TechDraw::DrawViewDimension] Dimension006
  Arbitrary = false
  ArbitraryTolerances = false
  EqualTolerance = true
  FormatSpec = %.2f
  FormatSpecOverTolerance = %+.2f
  FormatSpecUnderTolerance = %+.2f
  Inverted = false
  LockPosition = false
  MeasureType = 1
  OverTolerance = 0
  References2D = -> [ProjItem]
  Rotation = 0
  ScaleType = 0
  TheoreticalExact = false
  Type = 2
  UnderTolerance = 0
  X = 6.67068
  Y = 16.1167
FEATURE [TechDraw::DrawViewDimension] Dimension007
  Arbitrary = false
  ArbitraryTolerances = false
  EqualTolerance = true
  FormatSpec = %.2f
  FormatSpecOverTolerance = %+.2f
  FormatSpecUnderTolerance = %+.2f
  Inverted = false
  LockPosition = false
  MeasureType = 1
  OverTolerance = 0
  References2D = -> [ProjItem]
  Rotation = 0
  ScaleType = 0
  TheoreticalExact = false
  Type = 2
  UnderTolerance = 0
  X = 10.1981
  Y = -0.95012
FEATURE [TechDraw::DrawViewDimension] Dimension009
  Arbitrary = false
  ArbitraryTolerances = false
  EqualTolerance = true
  FormatSpec = %.2f
  FormatSpecOverTolerance = %+.2f
  FormatSpecUnderTolerance = %+.2f
  Inverted = false
  LockPosition = false
  MeasureType = 1
  OverTolerance = 0
  References2D = -> [ProjItem]
  Rotation = 0
  ScaleType = 0
  TheoreticalExact = false
  Type = 1
  UnderTolerance = 0
  X = 0
  Y = -2.21758
FEATURE [TechDraw::DrawViewDimension] Dimension010
  Arbitrary = false
  ArbitraryTolerances = false
  EqualTolerance = true
  FormatSpec = %.2f
  FormatSpecOverTolerance = %+.2f
  FormatSpecUnderTolerance = %+.2f
  Inverted = false
  LockPosition = false
  MeasureType = 1
  OverTolerance = 0
  References2D = -> [ProjItem]
  Rotation = 0
  ScaleType = 0
  TheoreticalExact = false
  Type = 1
  UnderTolerance = 0
  X = 0.099286
  Y = -12.9406
FEATURE [TechDraw::DrawViewDimension] Dimension011
  Arbitrary = false
  ArbitraryTolerances = false
  EqualTolerance = true
  FormatSpec = %.2f
  FormatSpecOverTolerance = %+.2f
  FormatSpecUnderTolerance = %+.2f
  Inverted = false
  LockPosition = false
  MeasureType = 1
  OverTolerance = 0
  References2D = -> [ProjItem]
  Rotation = 0
  ScaleType = 0
  TheoreticalExact = false
  Type = 1
  UnderTolerance = 0
  X = 4.95722
  Y = 7.24022
FEATURE [TechDraw::DrawViewDimension] Dimension013
  Arbitrary = false
  ArbitraryTolerances = false
  EqualTolerance = true
  FormatSpec = %.2f
  FormatSpecOverTolerance = %+.2f
  FormatSpecUnderTolerance = %+.2f
  Inverted = false
  LockPosition = false
  MeasureType = 1
  OverTolerance = 0
  References2D = -> [ProjItem004]
  Rotation = 0
  ScaleType = 0
  TheoreticalExact = false
  Type = 2
  UnderTolerance = 0
  X = -18.0371
  Y = 0
FEATURE [TechDraw::DrawViewDimension] Dimension014
  Arbitrary = false
  ArbitraryTolerances = false
  EqualTolerance = true
  FormatSpec = %.2f
  FormatSpecOverTolerance = %+.2f
  FormatSpecUnderTolerance = %+.2f
  Inverted = false
  LockPosition = false
  MeasureType = 1
  OverTolerance = 0
  References2D = -> [ProjItem004]
  Rotation = 0
  ScaleType = 0
  TheoreticalExact = false
  Type = 1
  UnderTolerance = 0
  X = 0.206079
  Y = 11.0845
FEATURE [TechDraw::DrawViewDimension] Dimension015
  Arbitrary = false
  ArbitraryTolerances = false
  EqualTolerance = true
  FormatSpec = %.2f
  FormatSpecOverTolerance = %+.2f
  FormatSpecUnderTolerance = %+.2f
  Inverted = false
  LockPosition = false
  MeasureType = 1
  OverTolerance = 0
  References2D = -> [ProjItem005]
  Rotation = 0
  ScaleType = 0
  TheoreticalExact = false
  Type = 2
  UnderTolerance = 0
  X = 16.2318
  Y = -0.296754
FEATURE [TechDraw::DrawViewDimension] Dimension016
  Arbitrary = false
  ArbitraryTolerances = false
  EqualTolerance = true
  FormatSpec = %.2f
  FormatSpecOverTolerance = %+.2f
  FormatSpecUnderTolerance = %+.2f
  Inverted = false
  LockPosition = false
  MeasureType = 1
  OverTolerance = 0
  References2D = -> [ProjItem009]
  Rotation = 0
  ScaleType = 0
  TheoreticalExact = false
  Type = 1
  UnderTolerance = 0
  X = 0
  Y = -26.1283
FEATURE [TechDraw::DrawViewDimension] Dimension017
  Arbitrary = false
  ArbitraryTolerances = false
  EqualTolerance = true
  FormatSpec = %.2f
  FormatSpecOverTolerance = %+.2f
  FormatSpecUnderTolerance = %+.2f
  Inverted = false
  LockPosition = false
  MeasureType = 1
  OverTolerance = 0
  References2D = -> [ProjItem009]
  Rotation = 0
  ScaleType = 0
  TheoreticalExact = false
  Type = 2
  UnderTolerance = 0
  X = -20.612
  Y = 1.73106
FEATURE [TechDraw::DrawViewDimension] Dimension019
  Arbitrary = false
  ArbitraryTolerances = false
  EqualTolerance = true
  FormatSpec = ⌀%.2f
  FormatSpecOverTolerance = %+.2f
  FormatSpecUnderTolerance = %+.2f
  Inverted = false
  LockPosition = false
  MeasureType = 1
  OverTolerance = 0
  References2D = -> [ProjItem009]
  Rotation = 0
  ScaleType = 0
  TheoreticalExact = false
  Type = 5
  UnderTolerance = 0
  X = 2.96754
  Y = -7.17155
FEATURE [TechDraw::DrawViewDimension] Dimension020
  Arbitrary = false
  ArbitraryTolerances = false
  EqualTolerance = true
  FormatSpec = ⌀%.2f
  FormatSpecOverTolerance = %+.2f
  FormatSpecUnderTolerance = %+.2f
  Inverted = false
  LockPosition = false
  MeasureType = 1
  OverTolerance = 0
  References2D = -> [ProjItem007]
  Rotation = 0
  ScaleType = 0
  TheoreticalExact = false
  Type = 5
  UnderTolerance = 0
  X = -9.14991
  Y = -5.44048
FEATURE [TechDraw::DrawViewDimension] Dimension021
  Arbitrary = false
  ArbitraryTolerances = false
  EqualTolerance = true
  FormatSpec = %.2f
  FormatSpecOverTolerance = %+.2f
  FormatSpecUnderTolerance = %+.2f
  Inverted = false
  LockPosition = false
  MeasureType = 1
  OverTolerance = 0
  References2D = -> [ProjItem007]
  Rotation = 0
  ScaleType = 0
  TheoreticalExact = false
  Type = 2
  UnderTolerance = 0
  X = -26
  Y = 0
FEATURE [TechDraw::DrawViewDimension] Dimension022
  Arbitrary = false
  ArbitraryTolerances = false
  EqualTolerance = true
  FormatSpec = %.2f
  FormatSpecOverTolerance = %+.2f
  FormatSpecUnderTolerance = %+.2f
  Inverted = false
  LockPosition = false
  MeasureType = 1
  OverTolerance = 0
  References2D = -> [ProjItem007]
  Rotation = 0
  ScaleType = 0
  TheoreticalExact = false
  Type = 2
  UnderTolerance = 0
  X = -35.8918
  Y = 0
FEATURE [TechDraw::DrawViewDimension] Dimension023
  Arbitrary = false
  ArbitraryTolerances = false
  EqualTolerance = true
  FormatSpec = %.2f
  FormatSpecOverTolerance = %+.2f
  FormatSpecUnderTolerance = %+.2f
  Inverted = false
  LockPosition = false
  MeasureType = 1
  OverTolerance = 0
  References2D = -> [ProjItem007]
  Rotation = 0
  ScaleType = 0
  TheoreticalExact = false
  Type = 1
  UnderTolerance = 0
  X = -0.49459
  Y = -17.7202
FEATURE [TechDraw::DrawViewDimension] Dimension024
  Arbitrary = false
  ArbitraryTolerances = false
  EqualTolerance = true
  FormatSpec = ⌀%.2f
  FormatSpecOverTolerance = %+.2f
  FormatSpecUnderTolerance = %+.2f
  Inverted = false
  LockPosition = false
  MeasureType = 1
  OverTolerance = 0
  References2D = -> [ProjItem007]
  Rotation = 0
  ScaleType = 0
  TheoreticalExact = false
  Type = 5
  UnderTolerance = 0
  X = 3.21483
  Y = 9.3972
FEATURE [TechDraw::DrawViewDimension] Dimension025
  Arbitrary = false
  ArbitraryTolerances = false
  EqualTolerance = true
  FormatSpec = %.2f
  FormatSpecOverTolerance = %+.2f
  FormatSpecUnderTolerance = %+.2f
  Inverted = false
  LockPosition = false
  MeasureType = 1
  OverTolerance = 0
  References2D = -> [ProjItem007]
  Rotation = 0
  ScaleType = 0
  TheoreticalExact = false
  Type = 2
  UnderTolerance = 0
  X = 31.6229
  Y = 1.23647
FEATURE [TechDraw::DrawViewDimension] Dimension026
  Arbitrary = false
  ArbitraryTolerances = false
  EqualTolerance = true
  FormatSpec = %.2f
  FormatSpecOverTolerance = %+.2f
  FormatSpecUnderTolerance = %+.2f
  Inverted = false
  LockPosition = false
  MeasureType = 1
  OverTolerance = 0
  References2D = -> [ProjItem007]
  Rotation = 0
  ScaleType = 0
  TheoreticalExact = false
  Type = 2
  UnderTolerance = 0
  X = 31.9351
  Y = 12.4811
FEATURE [TechDraw::DrawViewDimension] Dimension027
  Arbitrary = false
  ArbitraryTolerances = false
  EqualTolerance = true
  FormatSpec = %.2f
  FormatSpecOverTolerance = %+.2f
  FormatSpecUnderTolerance = %+.2f
  Inverted = false
  LockPosition = false
  MeasureType = 1
  OverTolerance = 0
  References2D = -> [ProjItem007]
  Rotation = 0
  ScaleType = 0
  TheoreticalExact = false
  Type = 2
  UnderTolerance = 0
  X = 31.6878
  Y = -10.75
FEATURE [TechDraw::DrawViewDimension] Dimension028
  Arbitrary = false
  ArbitraryTolerances = false
  EqualTolerance = true
  FormatSpec = %.2f
  FormatSpecOverTolerance = %+.2f
  FormatSpecUnderTolerance = %+.2f
  Inverted = false
  LockPosition = false
  MeasureType = 1
  OverTolerance = 0
  References2D = -> [ProjItem007]
  Rotation = 0
  ScaleType = 0
  TheoreticalExact = false
  Type = 1
  UnderTolerance = 0
  X = 9.89338
  Y = -6.00541
FEATURE [TechDraw::DrawViewDimension] Dimension030
  Arbitrary = false
  ArbitraryTolerances = false
  EqualTolerance = true
  FormatSpec = %.2f
  FormatSpecOverTolerance = %+.2f
  FormatSpecUnderTolerance = %+.2f
  Inverted = false
  LockPosition = false
  MeasureType = 1
  OverTolerance = 0
  References2D = -> [ProjItem002]
  Rotation = 0
  ScaleType = 0
  TheoreticalExact = false
  Type = 2
  UnderTolerance = 0
  X = -32.7724
  Y = -0.225748
FEATURE [TechDraw::DrawViewDimension] Dimension031
  Arbitrary = false
  ArbitraryTolerances = false
  EqualTolerance = true
  FormatSpec = %.2f
  FormatSpecOverTolerance = %+.2f
  FormatSpecUnderTolerance = %+.2f
  Inverted = false
  LockPosition = false
  MeasureType = 1
  OverTolerance = 0
  References2D = -> [ProjItem007]
  Rotation = 0
  ScaleType = 0
  TheoreticalExact = false
  Type = 1
  UnderTolerance = 0
  X = -27.418
  Y = 24.3808
FEATURE [TechDraw::DrawViewDimension] Dimension032
  Arbitrary = false
  ArbitraryTolerances = false
  EqualTolerance = true
  FormatSpec = %.2f
  FormatSpecOverTolerance = %+.2f
  FormatSpecUnderTolerance = %+.2f
  Inverted = false
  LockPosition = false
  MeasureType = 1
  OverTolerance = 0
  References2D = -> [ProjItem007]
  Rotation = 0
  ScaleType = 0
  TheoreticalExact = false
  Type = 2
  UnderTolerance = 0
  X = 9.54128
  Y = 27.3658
FEATURE [TechDraw::DrawViewDimension] Dimension033
  Arbitrary = false
  ArbitraryTolerances = false
  EqualTolerance = true
  FormatSpec = %.2f
  FormatSpecOverTolerance = %+.2f
  FormatSpecUnderTolerance = %+.2f
  Inverted = false
  LockPosition = false
  MeasureType = 1
  OverTolerance = 0
  References2D = -> [ProjItem007]
  Rotation = 0
  ScaleType = 0
  TheoreticalExact = false
  Type = 1
  UnderTolerance = 0
  X = -11
  Y = 24.6066
FEATURE [TechDraw::DrawViewDimension] Dimension034
  Arbitrary = false
  ArbitraryTolerances = false
  EqualTolerance = true
  FormatSpec = %.2f
  FormatSpecOverTolerance = %+.2f
  FormatSpecUnderTolerance = %+.2f
  Inverted = false
  LockPosition = false
  MeasureType = 1
  OverTolerance = 0
  References2D = -> [ProjItem007]
  Rotation = 0
  ScaleType = 0
  TheoreticalExact = false
  Type = 1
  UnderTolerance = 0
  X = 4.5
  Y = -9e-16
FEATURE [TechDraw::DrawViewDimension] Dimension035
  Arbitrary = false
  ArbitraryTolerances = false
  EqualTolerance = true
  FormatSpec = %.2f
  FormatSpecOverTolerance = %+.2f
  FormatSpecUnderTolerance = %+.2f
  Inverted = false
  LockPosition = false
  MeasureType = 1
  OverTolerance = 0
  References2D = -> [ProjItem007]
  Rotation = 0
  ScaleType = 0
  TheoreticalExact = false
  Type = 1
  UnderTolerance = 0
  X = 2.46827
  Y = 24.3808
FEATURE [TechDraw::DrawViewDimension] Dimension036
  Arbitrary = false
  ArbitraryTolerances = false
  EqualTolerance = true
  FormatSpec = %.2f
  FormatSpecOverTolerance = %+.2f
  FormatSpecUnderTolerance = %+.2f
  Inverted = false
  LockPosition = false
  MeasureType = 1
  OverTolerance = 0
  References2D = -> [ProjItem007]
  Rotation = 0
  ScaleType = 0
  TheoreticalExact = false
  Type = 1
  UnderTolerance = 0
  X = 19.6605
  Y = 24.1551
FEATURE [TechDraw::DrawViewDimension] Dimension037
  Arbitrary = false
  ArbitraryTolerances = false
  EqualTolerance = true
  FormatSpec = %.2f
  FormatSpecOverTolerance = %+.2f
  FormatSpecUnderTolerance = %+.2f
  Inverted = false
  LockPosition = false
  MeasureType = 1
  OverTolerance = 0
  References2D = -> [ProjItem002]
  Rotation = 0
  ScaleType = 0
  TheoreticalExact = false
  Type = 1
  UnderTolerance = 0
  X = -18.5
  Y = -0.343465
FEATURE [TechDraw::DrawViewDimension] Dimension038
  Arbitrary = false
  ArbitraryTolerances = false
  EqualTolerance = true
  FormatSpec = %.2f
  FormatSpecOverTolerance = %+.2f
  FormatSpecUnderTolerance = %+.2f
  Inverted = false
  LockPosition = false
  MeasureType = 1
  OverTolerance = 0
  References2D = -> [ProjItem002]
  Rotation = 0
  ScaleType = 0
  TheoreticalExact = false
  Type = 1
  UnderTolerance = 0
  X = -3.82827
  Y = -0.68693
FEATURE [TechDraw::DrawViewDimension] Dimension039
  Arbitrary = false
  ArbitraryTolerances = false
  EqualTolerance = true
  FormatSpec = %.2f
  FormatSpecOverTolerance = %+.2f
  FormatSpecUnderTolerance = %+.2f
  Inverted = false
  LockPosition = false
  MeasureType = 1
  OverTolerance = 0
  References2D = -> [ProjItem002]
  Rotation = 0
  ScaleType = 0
  TheoreticalExact = false
  Type = 1
  UnderTolerance = 0
  X = 14.5
  Y = 8.9e-15
FEATURE [TechDraw::DrawViewDimension] Dimension040
  Arbitrary = false
  ArbitraryTolerances = false
  EqualTolerance = true
  FormatSpec = %.2f
  FormatSpecOverTolerance = %+.2f
  FormatSpecUnderTolerance = %+.2f
  Inverted = false
  LockPosition = false
  MeasureType = 1
  OverTolerance = 0
  References2D = -> [ProjItem006]
  Rotation = 0
  ScaleType = 0
  TheoreticalExact = false
  Type = 1
  UnderTolerance = 0
  X = 0
  Y = -17.0608
FEATURE [TechDraw::DrawViewDimension] Dimension041
  Arbitrary = false
  ArbitraryTolerances = false
  EqualTolerance = true
  FormatSpec = %.2f
  FormatSpecOverTolerance = %+.2f
  FormatSpecUnderTolerance = %+.2f
  Inverted = false
  LockPosition = false
  MeasureType = 1
  OverTolerance = 0
  References2D = -> [ProjItem006]
  Rotation = 0
  ScaleType = 0
  TheoreticalExact = false
  Type = 2
  UnderTolerance = 0
  X = -43.5866
  Y = 1.03039
FEATURE [TechDraw::DrawViewDimension] Dimension042
  Arbitrary = false
  ArbitraryTolerances = false
  EqualTolerance = true
  FormatSpec = %.2f
  FormatSpecOverTolerance = %+.2f
  FormatSpecUnderTolerance = %+.2f
  Inverted = false
  LockPosition = false
  MeasureType = 1
  OverTolerance = 0
  References2D = -> [ProjItem006]
  Rotation = 0
  ScaleType = 0
  TheoreticalExact = false
  Type = 1
  UnderTolerance = 0
  X = -20.5375
  Y = -5.26746
FEATURE [TechDraw::DrawViewDimension] Dimension043
  Arbitrary = false
  ArbitraryTolerances = false
  EqualTolerance = true
  FormatSpec = %.2f
  FormatSpecOverTolerance = %+.2f
  FormatSpecUnderTolerance = %+.2f
  Inverted = false
  LockPosition = false
  MeasureType = 1
  OverTolerance = 0
  References2D = -> [ProjItem006]
  Rotation = 0
  ScaleType = 0
  TheoreticalExact = false
  Type = 1
  UnderTolerance = 0
  X = 32
  Y = 4.52695
FEATURE [TechDraw::DrawViewDimension] Dimension044
  Arbitrary = false
  ArbitraryTolerances = false
  EqualTolerance = true
  FormatSpec = %.2f
  FormatSpecOverTolerance = %+.2f
  FormatSpecUnderTolerance = %+.2f
  Inverted = false
  LockPosition = false
  MeasureType = 1
  OverTolerance = 0
  References2D = -> [ProjItem006]
  Rotation = 0
  ScaleType = 0
  TheoreticalExact = false
  Type = 1
  UnderTolerance = 0
  X = 41.0299
  Y = -14.0698
FEATURE [TechDraw::DrawViewDimension] Dimension045
  Arbitrary = false
  ArbitraryTolerances = false
  EqualTolerance = true
  FormatSpec = %.2f
  FormatSpecOverTolerance = %+.2f
  FormatSpecUnderTolerance = %+.2f
  Inverted = false
  LockPosition = false
  MeasureType = 1
  OverTolerance = 0
  References2D = -> [ProjItem006]
  Rotation = 0
  ScaleType = 0
  TheoreticalExact = false
  Type = 2
  UnderTolerance = 0
  X = 15.1394
  Y = 0.517616
FEATURE [TechDraw::DrawViewDimension] Dimension046
  Arbitrary = false
  ArbitraryTolerances = false
  EqualTolerance = true
  FormatSpec = %.2f
  FormatSpecOverTolerance = %+.2f
  FormatSpecUnderTolerance = %+.2f
  Inverted = false
  LockPosition = false
  MeasureType = 1
  OverTolerance = 0
  References2D = -> [ProjItem006]
  Rotation = 0
  ScaleType = 0
  TheoreticalExact = false
  Type = 2
  UnderTolerance = 0
  X = 14.1042
  Y = 10.9425
FEATURE [TechDraw::DrawViewDimension] Dimension047
  Arbitrary = false
  ArbitraryTolerances = false
  EqualTolerance = true
  FormatSpec = %.2f
  FormatSpecOverTolerance = %+.2f
  FormatSpecUnderTolerance = %+.2f
  Inverted = false
  LockPosition = false
  MeasureType = 1
  OverTolerance = 0
  References2D = -> [ProjItem006]
  Rotation = 0
  ScaleType = 0
  TheoreticalExact = false
  Type = 2
  UnderTolerance = 0
  X = 13.927
  Y = -9.17799
FEATURE [App::MeasureDistance] Distance  label="Distance: 5,24 mm"
  Distance = 5.23831
  P1 = (25.4145,-15,21.2333)
  P2 = (25.6427,-15,16)
FEATURE [TechDraw::DrawProjGroupItem] ProjItem012  label="Front007"
  CoarseView = false
  Direction = (0,-1,0)
  Focus = 100
  HardHidden = false
  IsoCount = 0
  IsoHidden = false
  IsoVisible = false
  LockPosition = true
  Perspective = false
  Rotation = 0
  RotationVector = (1,0,0)
  ScaleType = 2
  SeamHidden = false
  SeamVisible = true
  SmoothHidden = false
  SmoothVisible = true
  Source = -> [Body001]
  Type = 0
  X = 0
  XDirection = (1,0,0)
  Y = 0
FEATURE [TechDraw::DrawProjGroup] ProjGroup007
  Anchor = -> ProjItem012
  AutoDistribute = true
  LockPosition = false
  ProjectionType = 0
  Rotation = 0
  ScaleType = 0
  Source = -> [Body001]
  Views = -> [ProjItem012]
  X = 118.899
  Y = 171.814
  spacingX = 15
  spacingY = 15
FEATURE [TechDraw::DrawViewDimension] Dimension048
  Arbitrary = false
  ArbitraryTolerances = false
  EqualTolerance = true
  FormatSpec = ⌀%.2f
  FormatSpecOverTolerance = %+.2f
  FormatSpecUnderTolerance = %+.2f
  Inverted = false
  LockPosition = false
  MeasureType = 1
  OverTolerance = 0
  References2D = -> [ProjItem006]
  Rotation = 0
  ScaleType = 0
  TheoreticalExact = false
  Type = 5
  UnderTolerance = 0
  X = -0.178715
  Y = 11.7953
FEATURE [TechDraw::DrawPage] Page
  KeepUpdated = true
  NextBalloonIndex = 1
  ProjectionType = 0
  Template = -> Template
  Views = -> [ProjGroup,ProjGroup001,ProjGroup002,ProjGroup003,ProjGroup004,ProjGroup005,ProjGroup006,Dimension,Dimension002,Dimension003,Dimension004,Dimension005,Dimension006,Dimension007,Dimension009,Dimension010,Dimension011,Dimension013,Dimension014,Dimension015,Dimension016,Dimension017,Dimension019,Dimension020,Dimension021,Dimension022,Dimension023,Dimension024,Dimension025,Dimension026,Dimension027,+21 more]
FEATURE [App::DocumentObjectGroup] Group  label="Чертежи"
  Group = -> [Page]
